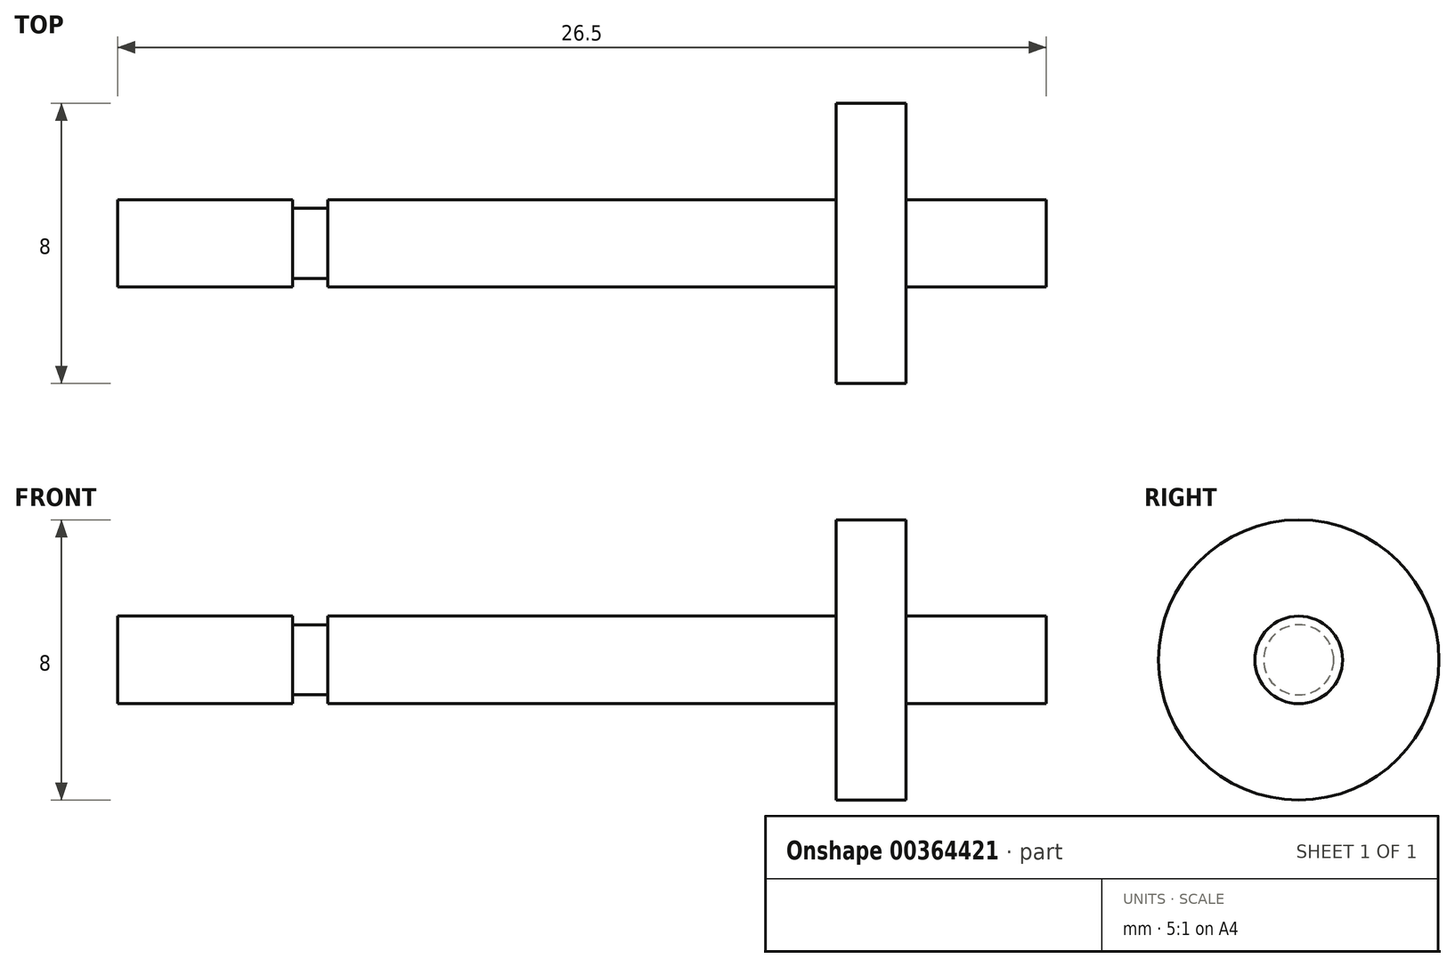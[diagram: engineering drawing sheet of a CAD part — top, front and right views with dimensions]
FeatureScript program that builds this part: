
annotation { "Feature Type Name" : "Feature", "Feature Type Description" : "" }
export const myFeature = defineFeature(function(context is Context, id is Id, definition is map)
    precondition{}
    {
        {
            var Q0;
            Q0=qCreatedBy(makeId("Front.planeOp"),FACE);
            var sketch = newSketch(context, id + "F0", { "sketchPlane" : qUnion([Q0])});
            skLineSegment(sketch, "E0", {"start": v(-16.9, 2.58) * mm, "end": v(9.6, 2.58) * mm});
            skLineSegment(sketch, "E1", {"start": v(9.6, 2.58) * mm, "end": v(9.6, 3.83) * mm});
            skLineSegment(sketch, "E2", {"start": v(9.6, 3.83) * mm, "end": v(5.6, 3.83) * mm});
            skLineSegment(sketch, "E3", {"start": v(5.6, 3.83) * mm, "end": v(5.6, 6.58) * mm});
            skLineSegment(sketch, "E4", {"start": v(5.6, 6.58) * mm, "end": v(3.6, 6.58) * mm});
            skLineSegment(sketch, "E5", {"start": v(3.6, 6.58) * mm, "end": v(3.6, 3.83) * mm});
            skLineSegment(sketch, "E6", {"start": v(3.6, 3.83) * mm, "end": v(-10.9, 3.83) * mm});
            skLineSegment(sketch, "E7", {"start": v(-10.9, 3.83) * mm, "end": v(-10.9, 3.58) * mm});
            skLineSegment(sketch, "E8", {"start": v(-10.9, 3.58) * mm, "end": v(-11.9, 3.58) * mm});
            skLineSegment(sketch, "E9", {"start": v(-11.9, 3.58) * mm, "end": v(-11.9, 3.83) * mm});
            skLineSegment(sketch, "E10", {"start": v(-11.9, 3.83) * mm, "end": v(-16.9, 3.83) * mm});
            skLineSegment(sketch, "E11", {"start": v(-16.9, 3.83) * mm, "end": v(-16.9, 2.58) * mm});
            skSolve(sketch);
        }
        {
            var Q0;
            Q0=sQuery(id+"F0.wireOp",EDGE,"E11");
            var Q1;
            Q1=sQuery(id+"F0.wireOp",EDGE,"E10");
            var Q2;
            Q2=sQuery(id+"F0.wireOp",EDGE,"E9");
            var Q3;
            Q3=sQuery(id+"F0.wireOp",EDGE,"E8");
            var Q4;
            Q4=sQuery(id+"F0.wireOp",EDGE,"E7");
            var Q5;
            Q5=sQuery(id+"F0.wireOp",EDGE,"E6");
            var Q6;
            Q6=sQuery(id+"F0.wireOp",EDGE,"E5");
            var Q7;
            Q7=sQuery(id+"F0.wireOp",EDGE,"E4");
            var Q8;
            Q8=sQuery(id+"F0.wireOp",EDGE,"E3");
            var Q9;
            Q9=sQuery(id+"F0.wireOp",EDGE,"E2");
            var Q10;
            Q10=sQuery(id+"F0.wireOp",EDGE,"E1");
            var Q11;
            Q11=sQuery(id+"F0.wireOp",EDGE,"E0");
            revolve(context, id + "F1", {"bodyType" : ToolBodyType.SURFACE, "surfaceEntities" : qUnion([Q0, Q1, Q2, Q3, Q4, Q5, Q6, Q7, Q8, Q9, Q10]), "axis" : qUnion([Q11]), "revolveType" : RevolveType.FULL});
        }
    });
